# Revit family: Diverter_Valve_Trim-American_Standard-Studio_S-T105.430
name_source: partatom
category: Plumbing Fixtures
revit_build: Autodesk Revit 2014 (Build: 20130308_1515(x64)
units: mm (PartAtom-declared; Revit-internal decimal feet)

## types (1)
- T105.430
    ADA Compliant = Yes
    Assembly Code = D2020300
    CW Connection = Yes
    CWFU = 3
    Connection Description = 1/2'' Water Connection Outlet
    Default Elevation = 40"
    Description = Studio S In-Wall Diverter Valve
    Finish = Metal-American Standard-002-Polished Chrome
    HW Connection = Yes
    HWFU = 3
    Height = 1 13/16"
    Installation Type = Wall Mounted
    Length = 4 3/16"
    Manufacturer = American Standard
    Material = Metal-American Standard-002-Polished Chrome
    Model = T105.430
    Price = Prices may vary. Please consult Manufacturer Representative for most up-to-date price list.
    Product Documentation Link = https://www.americanstandard-us.com
    Product Page URL = https://www.americanstandard-us.com
    R422 Two-Way In-Wall Diverter Valve Rough (Discrete) = No
    R422S Two-Way In-Wall Diverter Valve Rough (Shared) = No
    R433 Three-Way In-Wall Diverter Valve Rough (Discrete) = No
    R433S Three-Way In-Wall Diverter Valve Rough (Shared) = No
    Spacing from Wall = 2 3/4"
    Specification = Two (three) way diverter shall feature a forged brass body with 1/2" NPT mixed water inlet and outlets.
    Third Connection = 1/2"
    URL = https://www.americanstandard-us.com
    Vent Connection = No
    WFU = 4
    Warranty Information = One Year Limited Warranty
    Waste Connection = Yes
    Water Connection Diameter = 1/2"
    Water Connection Radius = 1/4"
    Width = 2 3/4"

## geometry (parser evidence)
native form markers: Sweep x3
no freeform markers — native parametric forms only
